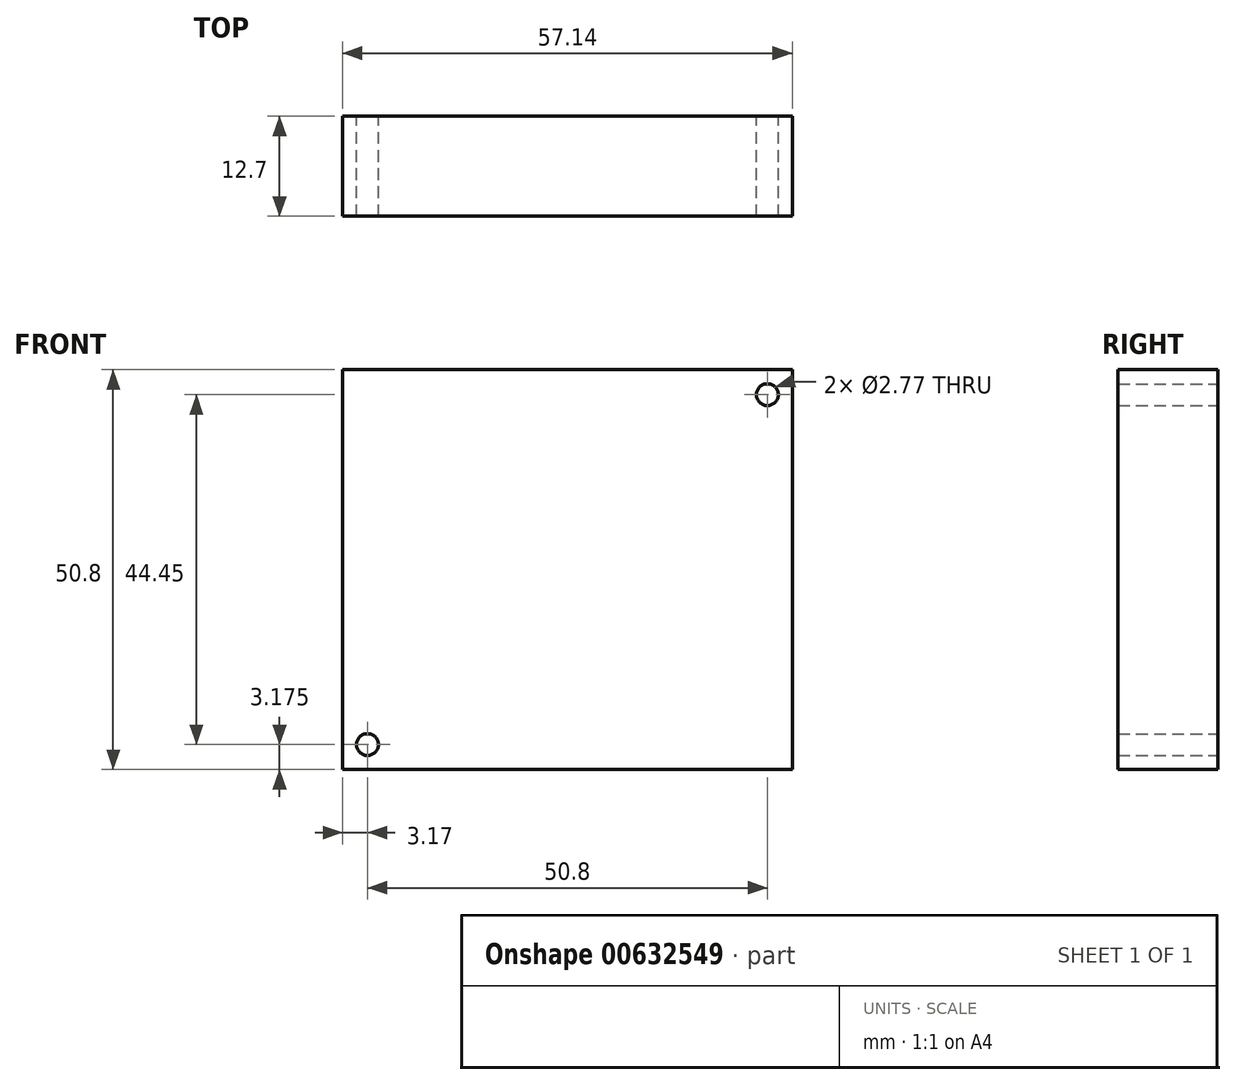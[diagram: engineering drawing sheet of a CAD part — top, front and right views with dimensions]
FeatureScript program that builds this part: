
annotation { "Feature Type Name" : "Feature", "Feature Type Description" : "" }
export const myFeature = defineFeature(function(context is Context, id is Id, definition is map)
    precondition{}
    {
        {
            var Q0;
            Q0=qCreatedBy(makeId("Front.planeOp"),FACE);
            var sketch = newSketch(context, id + "F0", { "sketchPlane" : qUnion([Q0])});
            skLineSegment(sketch, "E0.bottom", {"start": v(28.58, 25.4) * mm, "end": v(-28.58, 25.4) * mm});
            skLineSegment(sketch, "E0.top", {"start": v(28.58, -25.4) * mm, "end": v(-28.58, -25.4) * mm});
            skLineSegment(sketch, "E0.left", {"start": v(28.58, 25.4) * mm, "end": v(28.58, -25.4) * mm});
            skLineSegment(sketch, "E0.right", {"start": v(-28.57, 25.4) * mm, "end": v(-28.58, -25.4) * mm});
            skPoint(sketch, "E0.middle", {"position": v(0, 0) * mm});
            skSolve(sketch);
        }
        {
            var Q0;
            Q0=makeQuery(id+"F0.imprint","IMPRINT",FACE,{"disambiguationData":[TD([[makeQuery(id+"F0.imprint","IMPRINT",EDGE,{"derivedFrom":sQuery(id+"F0.wireOp",EDGE,"E0.bottom")}),1.0]])]});
            extrude(context, id + "F1", {"entities" : qUnion([Q0]), "depth" : 12.7 * mm, "offsetDistance" : 25.4 * mm});
        }
        {
            var Q0;
            Q0=makeQuery(id+"F1.opExtrude","CAP_FACE",FACE,{"disambiguationData":[OSD([sQuery(id+"F0.wireOp",EDGE,"E0.bottom"),sQuery(id+"F0.wireOp",EDGE,"E0.top"),sQuery(id+"F0.wireOp",EDGE,"E0.left"),sQuery(id+"F0.wireOp",EDGE,"E0.right")])],"isStart":true});
            var sketch = newSketch(context, id + "F2", { "sketchPlane" : qUnion([Q0])});
            skPoint(sketch, "E1", {"position": v(25.4, 5.72) * mm});
            skPoint(sketch, "E2", {"position": v(25.4, -22.23) * mm});
            skPoint(sketch, "E3", {"position": v(-19.05, 5.71) * mm});
            skPoint(sketch, "E4", {"position": v(-25.4, 22.23) * mm});
            skSolve(sketch);
        }
        {
            var Q0;
            Q0=sQuery(id+"F2.wireOp",VERTEX,"E2");
            var Q1;
            Q1=sQuery(id+"F2.wireOp",VERTEX,"E4");
            var Q2;
            Q2=makeQuery(id+"F1.opExtrude","SWEPT_BODY",BODY,{"disambiguationData":[OSD([sQuery(id+"F0.wireOp",EDGE,"E0.bottom"),sQuery(id+"F0.wireOp",EDGE,"E0.top"),sQuery(id+"F0.wireOp",EDGE,"E0.left"),sQuery(id+"F0.wireOp",EDGE,"E0.right")])]});
            hole(context, id + "F3", {"style" : HoleStyle.SIMPLE, "endStyle" : HoleEndStyle.THROUGH, "holeDiameter" : 2.77 * mm, "majorDiameter" : 6.35 * mm, "isTappedThrough" : true, "tappedDepth" : 12.7 * mm, "tapClearance" : 3, "locations" : qUnion([Q0, Q1]), "scope" : qUnion([Q2])});
        }
    });
